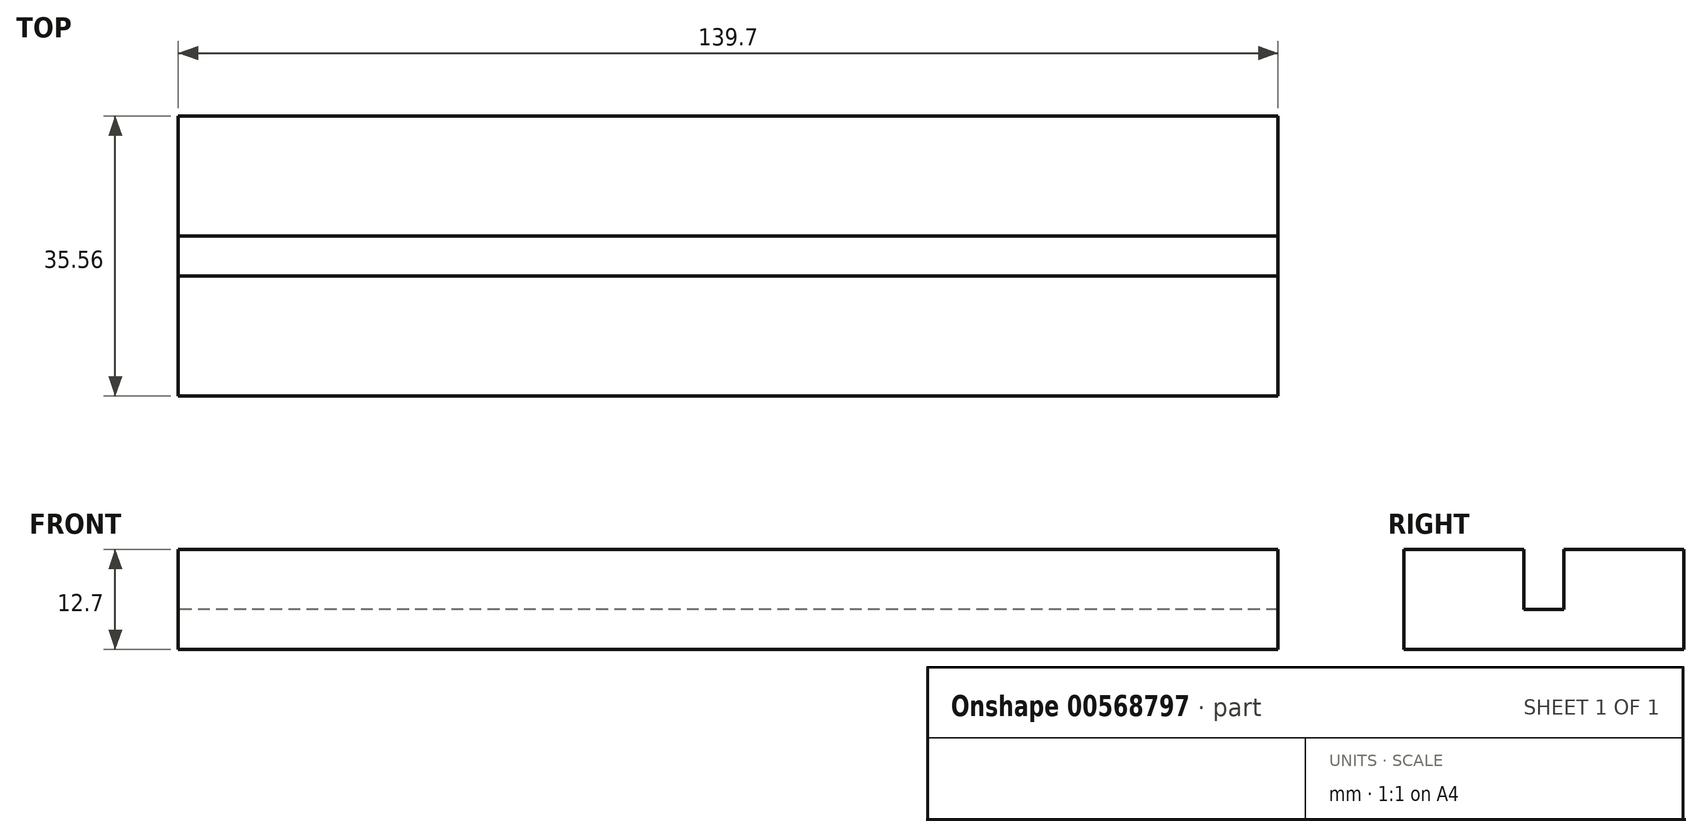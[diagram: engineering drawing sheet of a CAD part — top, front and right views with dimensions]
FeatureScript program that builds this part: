
annotation { "Feature Type Name" : "Feature", "Feature Type Description" : "" }
export const myFeature = defineFeature(function(context is Context, id is Id, definition is map)
    precondition{}
    {
        {
            var Q0;
            Q0=qCreatedBy(makeId("Right.planeOp"),FACE);
            var sketch = newSketch(context, id + "F0", { "sketchPlane" : qUnion([Q0])});
            skLineSegment(sketch, "E0", {"start": v(-19.57, 0) * mm, "end": v(15.99, 0) * mm});
            skLineSegment(sketch, "E1", {"start": v(-19.57, 0) * mm, "end": v(-19.57, 12.7) * mm});
            skLineSegment(sketch, "E2", {"start": v(-19.57, 12.7) * mm, "end": v(-4.33, 12.7) * mm});
            skLineSegment(sketch, "E3", {"start": v(-4.33, 12.7) * mm, "end": v(-4.33, 5.08) * mm});
            skLineSegment(sketch, "E4", {"start": v(-4.33, 5.08) * mm, "end": v(0.75, 5.08) * mm});
            skLineSegment(sketch, "E5", {"start": v(0.75, 5.08) * mm, "end": v(0.75, 12.7) * mm});
            skLineSegment(sketch, "E6", {"start": v(0.75, 12.7) * mm, "end": v(15.99, 12.7) * mm});
            skLineSegment(sketch, "E7", {"start": v(15.99, 12.7) * mm, "end": v(15.99, 0) * mm});
            skSolve(sketch);
        }
        {
            var Q0;
            Q0 = qSketchRegion(id + "F0", true);
            extrude(context, id + "F1", {"entities" : qUnion([Q0]), "depth" : 139.7 * mm, "offsetDistance" : 25.4 * mm});
        }
    });
